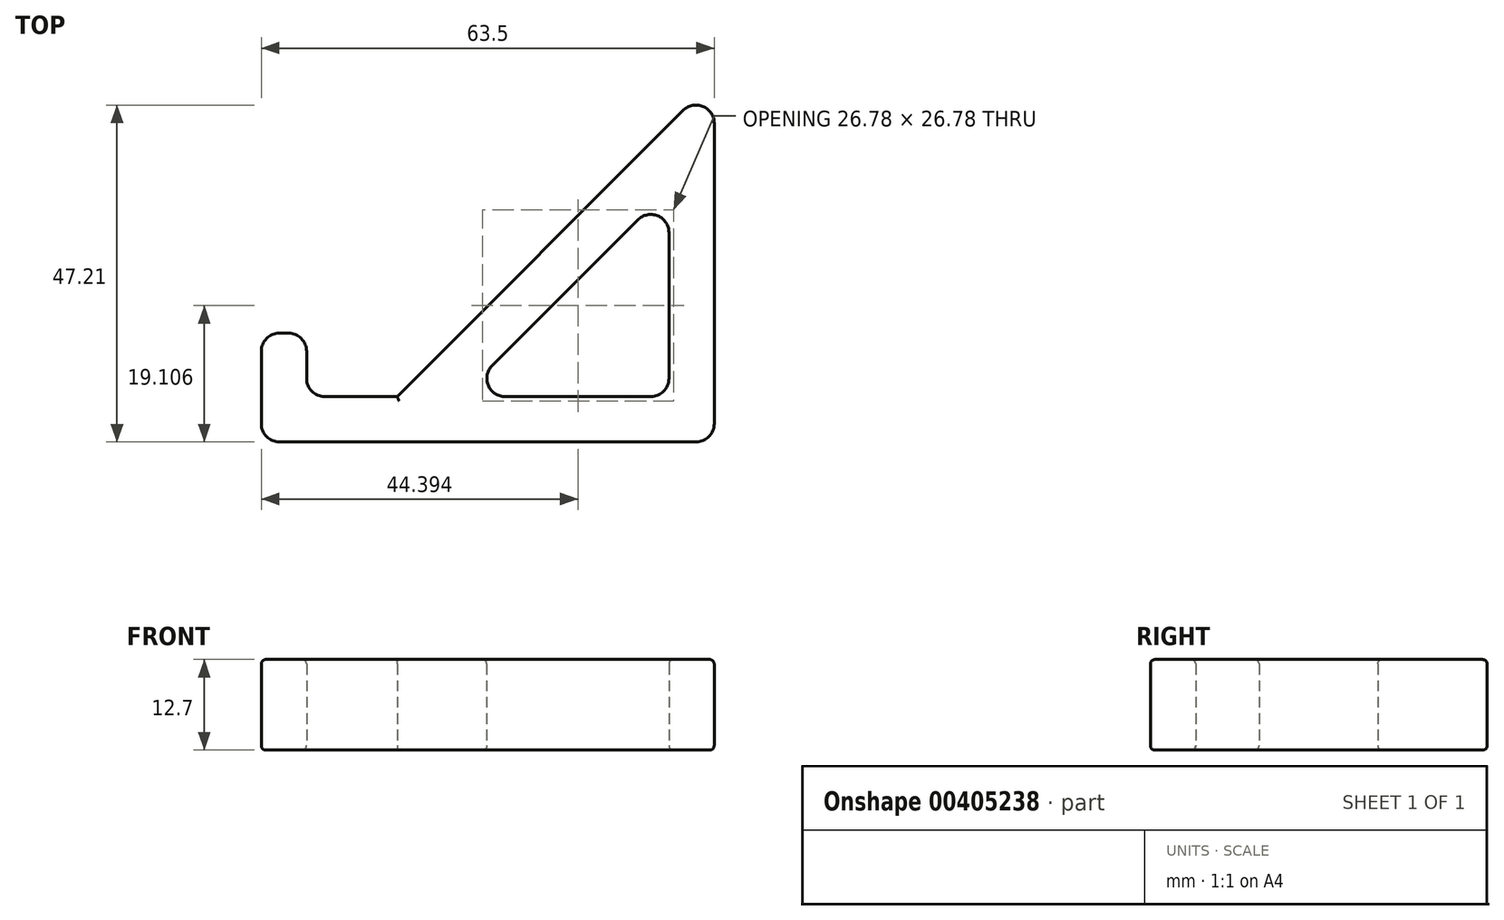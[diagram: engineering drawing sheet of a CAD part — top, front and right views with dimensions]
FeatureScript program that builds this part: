
annotation { "Feature Type Name" : "Feature", "Feature Type Description" : "" }
export const myFeature = defineFeature(function(context is Context, id is Id, definition is map)
    precondition{}
    {
        {
            var Q0;
            Q0=qCreatedBy(makeId("Top.planeOp"),FACE);
            var sketch = newSketch(context, id + "F0", { "sketchPlane" : qUnion([Q0])});
            skLineSegment(sketch, "E0.bottom", {"start": v(-2.54, 0) * mm, "end": v(-60.96, 0) * mm});
            skLineSegment(sketch, "E0.left", {"start": v(0, 2.54) * mm, "end": v(0, 6.35) * mm});
            skLineSegment(sketch, "E0.right", {"start": v(-63.5, 2.54) * mm, "end": v(-63.5, 6.35) * mm});
            skLineSegment(sketch, "E1.top", {"start": v(-60.96, 15.24) * mm, "end": v(-59.69, 15.24) * mm});
            skLineSegment(sketch, "E1.left", {"start": v(-63.5, 6.35) * mm, "end": v(-63.5, 12.7) * mm});
            skLineSegment(sketch, "E1.right", {"start": v(-57.15, 8.89) * mm, "end": v(-57.15, 12.7) * mm});
            skLineSegment(sketch, "E2.left", {"start": v(0, 6.35) * mm, "end": v(0, 44.67) * mm});
            skLineSegment(sketch, "E3", {"start": v(-44.45, 6.35) * mm, "end": v(-4.34, 46.46) * mm});
            skLineSegment(sketch, "E4", {"start": v(-10.69, 31.13) * mm, "end": v(-31.13, 10.69) * mm});
            skPoint(sketch, "E5.visualSharp", {"position": v(-63.5, 15.24) * mm});
            skArc(sketch, "E5.filletArc", {"start": v(-60.96, 15.24) * mm, "mid": v(-62.76, 14.5) * mm, "end": v(-63.5, 12.7) * mm});
            skPoint(sketch, "E6.visualSharp", {"position": v(-57.15, 15.24) * mm});
            skArc(sketch, "E6.filletArc", {"start": v(-57.15, 12.7) * mm, "mid": v(-57.9, 14.5) * mm, "end": v(-59.69, 15.24) * mm});
            skPoint(sketch, "E7.visualSharp", {"position": v(-57.15, 8.89) * mm});
            skArc(sketch, "E7.filletArc", {"start": v(-57.15, 8.89) * mm, "mid": v(-56.4, 7.1) * mm, "end": v(-54.6, 6.35) * mm});
            skPoint(sketch, "E8.visualSharp", {"position": v(-63.5, 0) * mm});
            skArc(sketch, "E8.filletArc", {"start": v(-63.5, 2.54) * mm, "mid": v(-62.76, 0.74) * mm, "end": v(-60.96, 0) * mm});
            skPoint(sketch, "E9.visualSharp", {"position": v(0, 0) * mm});
            skArc(sketch, "E9.filletArc", {"start": v(-2.54, 0) * mm, "mid": v(-0.74, 0.74) * mm, "end": v(0, 2.54) * mm});
            skLineSegment(sketch, "E10", {"start": v(-54.6, 6.35) * mm, "end": v(-44.45, 6.35) * mm});
            skLineSegment(sketch, "E11", {"start": v(-29.34, 6.35) * mm, "end": v(-8.9, 6.35) * mm});
            skLineSegment(sketch, "E12", {"start": v(-6.35, 29.34) * mm, "end": v(-6.35, 8.9) * mm});
            skPoint(sketch, "E13.visualSharp", {"position": v(0, 50.8) * mm});
            skArc(sketch, "E13.filletArc", {"start": v(0, 44.67) * mm, "mid": v(-1.57, 47.01) * mm, "end": v(-4.34, 46.46) * mm});
            skPoint(sketch, "E14.visualSharp", {"position": v(-6.35, 35.47) * mm});
            skArc(sketch, "E14.filletArc", {"start": v(-6.35, 29.34) * mm, "mid": v(-7.92, 31.68) * mm, "end": v(-10.69, 31.13) * mm});
            skPoint(sketch, "E15.visualSharp", {"position": v(-35.47, 6.35) * mm});
            skArc(sketch, "E15.filletArc", {"start": v(-31.13, 10.69) * mm, "mid": v(-31.68, 7.92) * mm, "end": v(-29.34, 6.35) * mm});
            skPoint(sketch, "E16.visualSharp", {"position": v(-6.35, 6.35) * mm});
            skArc(sketch, "E16.filletArc", {"start": v(-8.9, 6.35) * mm, "mid": v(-7.1, 7.1) * mm, "end": v(-6.35, 8.9) * mm});
            skSolve(sketch);
        }
        {
            var Q0;
            Q0 = qSketchRegion(id + "F0", true);
            extrude(context, id + "F1", {"entities" : qUnion([Q0]), "depth" : 12.7 * mm});
        }
        {
            var Q0;
            Q0=makeQuery(id+"F1.opExtrude","CAP_EDGE",EDGE,{"disambiguationData":[OSD([sQuery(id+"F0.wireOp",EDGE,"E3")])],"isStart":false});
            var Q1;
            Q1=makeQuery(id+"F1.opExtrude","CAP_EDGE",EDGE,{"disambiguationData":[OSD([sQuery(id+"F0.wireOp",EDGE,"E12")])],"isStart":false});
            var Q2;
            Q2=makeQuery(id+"F1.opExtrude","CAP_EDGE",EDGE,{"disambiguationData":[OSD([sQuery(id+"F0.wireOp",EDGE,"E3")])],"isStart":true});
            var Q3;
            Q3=makeQuery(id+"F1.opExtrude","CAP_EDGE",EDGE,{"disambiguationData":[OSD([sQuery(id+"F0.wireOp",EDGE,"E4")])],"isStart":true});
            fillet(context, id + "F2", {"entities" : qUnion([Q0, Q1, Q2, Q3]), "radius" : 0.64 * mm, "tangentPropagation" : true, "allowEdgeOverflow" : false});
        }
    });
